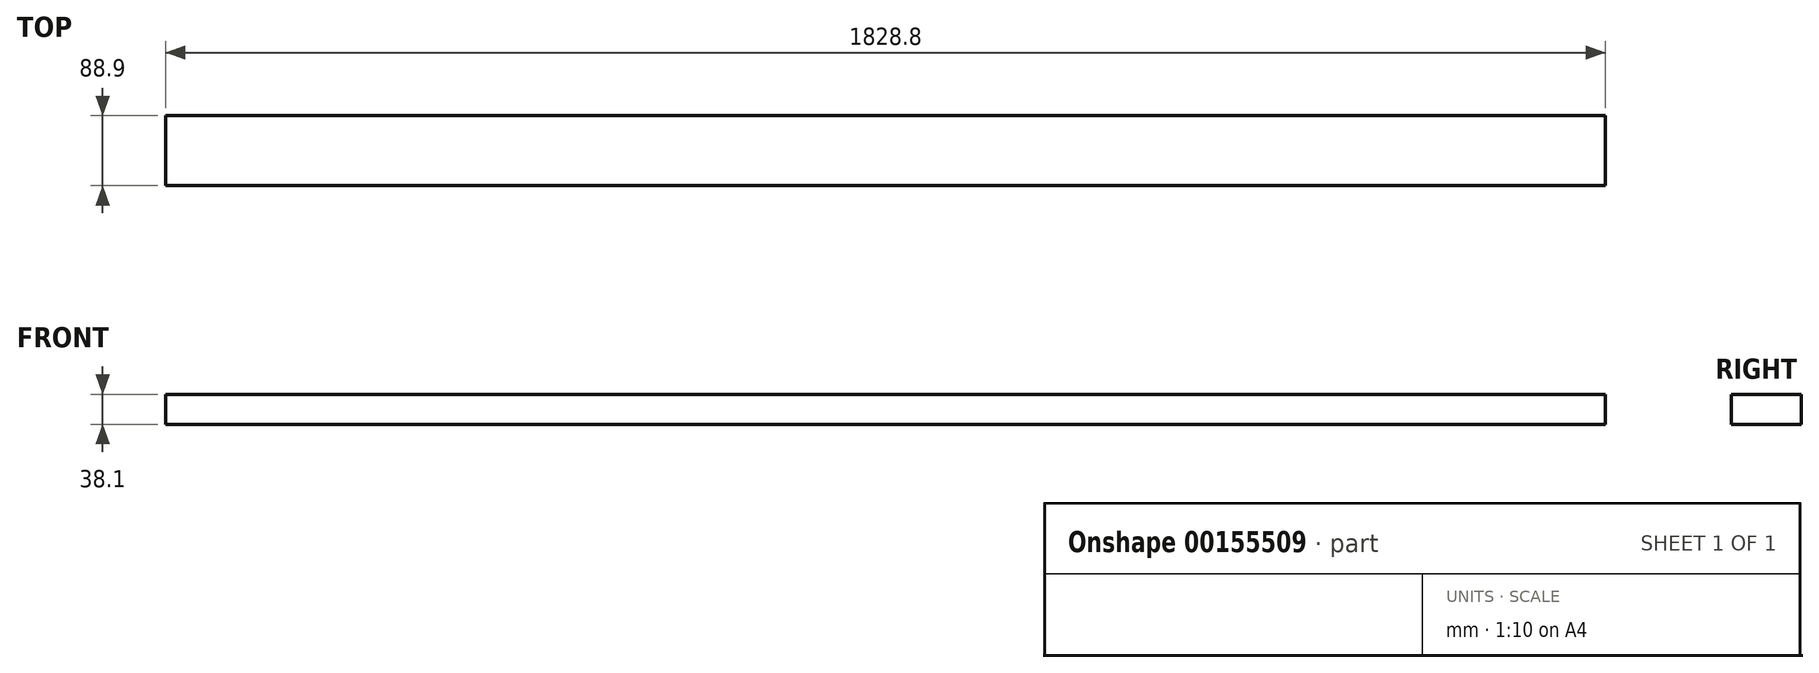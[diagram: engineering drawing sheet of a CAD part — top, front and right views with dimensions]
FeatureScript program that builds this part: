
annotation { "Feature Type Name" : "Feature", "Feature Type Description" : "" }
export const myFeature = defineFeature(function(context is Context, id is Id, definition is map)
    precondition{}
    {
        {
            var Q0;
            Q0=qCreatedBy(makeId("Top.planeOp"), FACE);
            var sketch = newSketch(context, id + "F0", { "sketchPlane" : qUnion([Q0])});
            skLineSegment(sketch, "E0.bottom", {"start": v(-1747.67, 69.17) * mm, "end": v(81.13, 69.17) * mm});
            skLineSegment(sketch, "E0.top", {"start": v(-1747.67, -19.73) * mm, "end": v(81.13, -19.73) * mm});
            skLineSegment(sketch, "E0.left", {"start": v(-1747.67, 69.17) * mm, "end": v(-1747.67, -19.73) * mm});
            skLineSegment(sketch, "E0.right", {"start": v(81.13, 69.17) * mm, "end": v(81.13, -19.73) * mm});
            skSolve(sketch);
        }
        {
            var Q0;
            Q0 = qSketchRegion(id + "F0", true);
            extrude(context, id + "F1", {"entities" : qUnion([Q0]), "domain" : OperationDomain.MODEL, "flatOperationType" : FlatOperationType.REMOVE, "depth" : 38.1 * mm, "offsetDistance" : 25.4 * mm});
        }
    });
